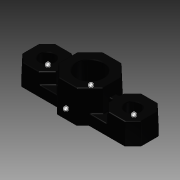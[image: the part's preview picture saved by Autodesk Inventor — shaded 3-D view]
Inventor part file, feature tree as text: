
AUTODESK INVENTOR PART (.ipt)
format: ipt  version: 2015 (Build 190159000, 159)  size: 720,384 bytes
history: native  units: in
note: dims shown in document units (in); Inventor stores cm internally (conversion verified against a paired STEP export)
features: fillet x1, other x1, imported_body x1
ambient origin geometry x8: Origin, YZ Plane, XZ Plane, XY Plane, X Axis, Y Axis, Z Axis, Center Point
bodies: Body1 (feature_tree)
feature tree (3):
  fillet  "Fillet7"  [1 undecoded]
  other  "Bearing Block HS"
  imported_body  "Base1"
note: 1 required parameter value undecoded (feature->parameter linkage not recoverable at this tier; creation-order binding heuristic only, values carry confidence <= 0.55)
